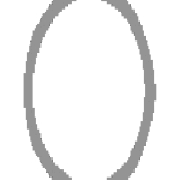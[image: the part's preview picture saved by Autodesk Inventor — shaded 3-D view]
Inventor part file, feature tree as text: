
AUTODESK INVENTOR PART (.ipt)
format: ipt  version: 2021 (Build 250183000, 183)  size: 111,104 bytes
history: native  units: in
note: dims shown in document units (in); Inventor stores cm internally (conversion verified against a paired STEP export)
features: other x4, sketch x3, plane x1
ambient origin geometry x8: Origin, YZ Plane, XZ Plane, XY Plane, X Axis, Y Axis, Z Axis, Center Point
bodies: Solid1 (feature_tree), Body (feature_tree)
feature tree (8):
  other  "Driven Length"
  other  "Frame Generator"
  other  "Start Plane"
  other  "End Plane"
  sketch  "Sketch"  dims[d2=38.7943in d4=-0.0in d5=38.7943in d6=0.12in d7=0.0in d8=90.0deg d9=38.7943in]
  sketch  "Sketch2"  dims[d0=1.0in]
  plane  "Work Plane3"
  sketch  "Sketch3"  dims[d1=0.065in]
